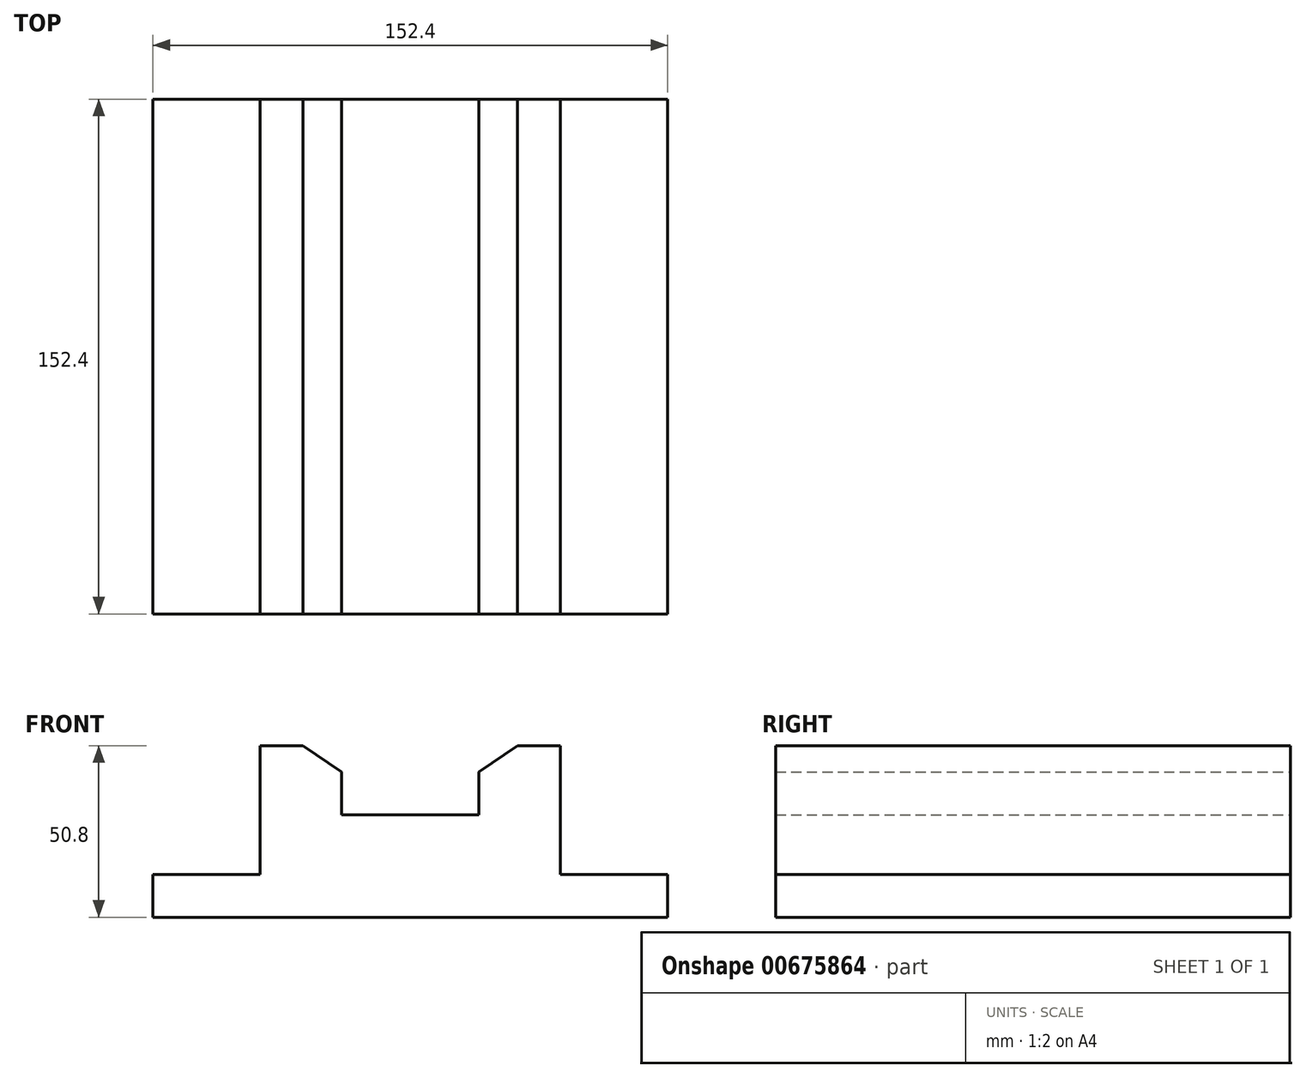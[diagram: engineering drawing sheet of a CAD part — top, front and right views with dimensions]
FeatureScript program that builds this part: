
annotation { "Feature Type Name" : "Feature", "Feature Type Description" : "" }
export const myFeature = defineFeature(function(context is Context, id is Id, definition is map)
    precondition{}
    {
        {
            var Q0;
            Q0=qCreatedBy(makeId("Front.planeOp"),FACE);
            var sketch = newSketch(context, id + "F0", { "sketchPlane" : qUnion([Q0])});
            skLineSegment(sketch, "E0", {"start": v(-96.5, -24.31) * mm, "end": v(-64.74, -24.31) * mm});
            skLineSegment(sketch, "E1", {"start": v(-64.74, -24.31) * mm, "end": v(-64.74, 13.79) * mm});
            skLineSegment(sketch, "E2", {"start": v(-64.74, 13.79) * mm, "end": v(-52.04, 13.79) * mm});
            skLineSegment(sketch, "E3", {"start": v(-52.04, 13.79) * mm, "end": v(-40.59, 5.94) * mm});
            skLineSegment(sketch, "E4", {"start": v(-40.59, 5.94) * mm, "end": v(-40.59, -6.76) * mm});
            skLineSegment(sketch, "E5", {"start": v(-40.59, -6.76) * mm, "end": v(0, -6.76) * mm});
            skLineSegment(sketch, "E6", {"start": v(0, -6.76) * mm, "end": v(0, 5.94) * mm});
            skLineSegment(sketch, "E7", {"start": v(0, 5.94) * mm, "end": v(11.46, 13.79) * mm});
            skLineSegment(sketch, "E8", {"start": v(11.46, 13.79) * mm, "end": v(24.16, 13.79) * mm});
            skLineSegment(sketch, "E9", {"start": v(24.16, 13.79) * mm, "end": v(24.16, -24.31) * mm});
            skLineSegment(sketch, "E10", {"start": v(24.16, -24.31) * mm, "end": v(55.9, -24.31) * mm});
            skLineSegment(sketch, "E11", {"start": v(55.9, -24.31) * mm, "end": v(55.9, -37.01) * mm});
            skLineSegment(sketch, "E12", {"start": v(55.9, -37.01) * mm, "end": v(-96.5, -37.01) * mm});
            skLineSegment(sketch, "E13", {"start": v(-96.5, -37.01) * mm, "end": v(-96.5, -24.31) * mm});
            skSolve(sketch);
        }
        {
            var Q0;
            Q0=makeQuery(id+"F0.imprint","IMPRINT",FACE,{"disambiguationData":[TD([[makeQuery(id+"F0.imprint","IMPRINT",EDGE,{"derivedFrom":sQuery(id+"F0.wireOp",EDGE,"E0")}),-1.0]])]});
            extrude(context, id + "F1", {"entities" : qUnion([Q0]), "depth" : 152.4 * mm, "offsetDistance" : 25.4 * mm});
        }
    });
